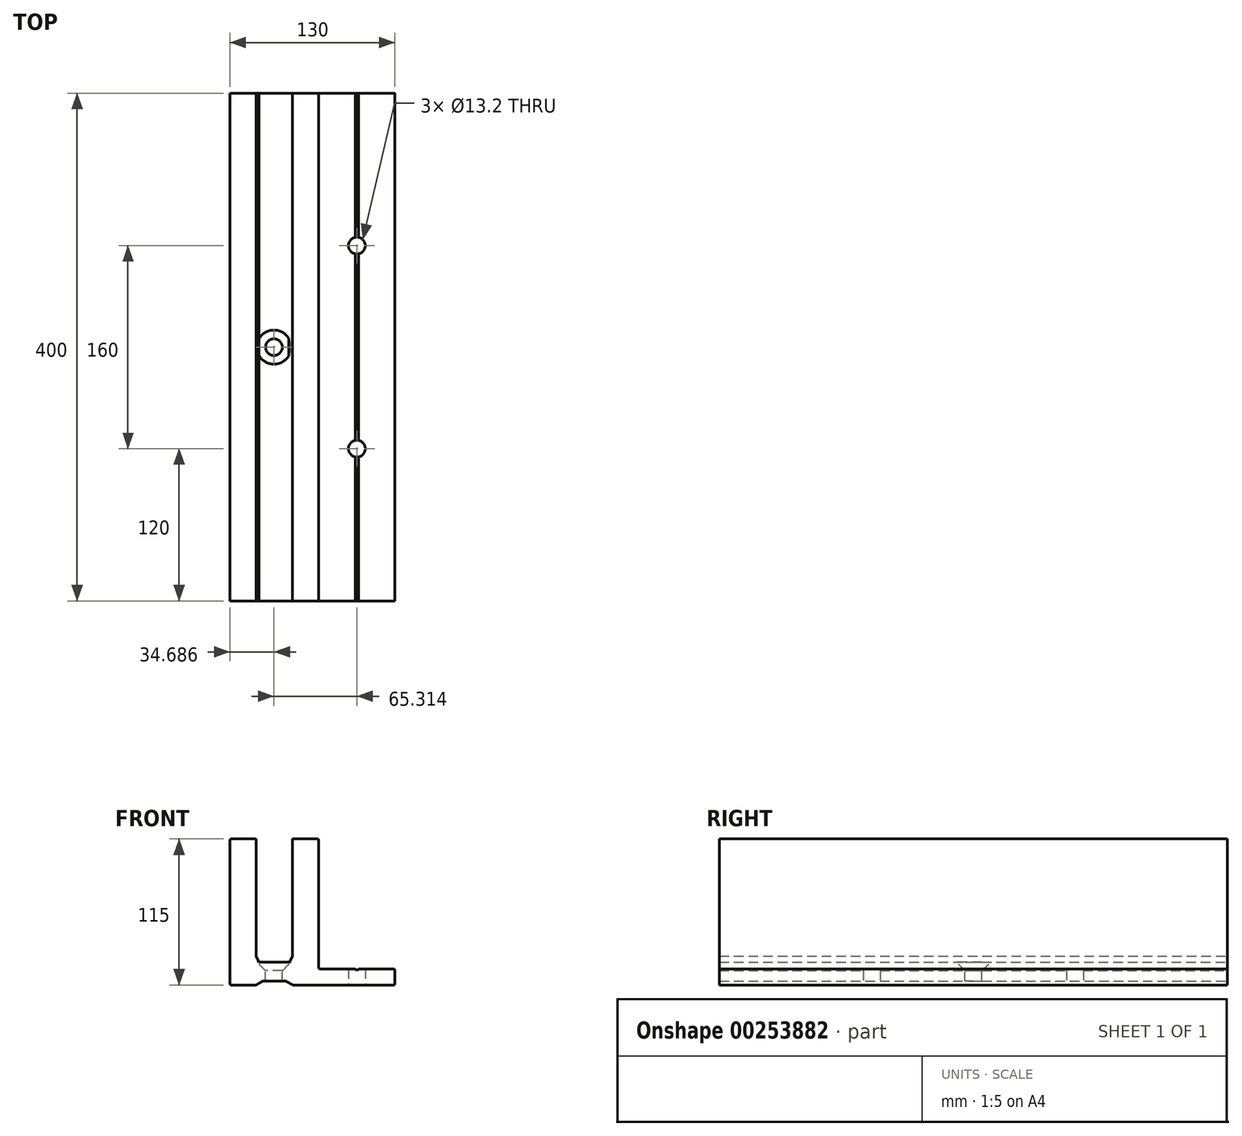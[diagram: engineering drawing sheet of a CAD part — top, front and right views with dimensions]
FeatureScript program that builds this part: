
annotation { "Feature Type Name" : "Feature", "Feature Type Description" : "" }
export const myFeature = defineFeature(function(context is Context, id is Id, definition is map)
    precondition{}
    {
        {
            var Q0;
            Q0=qCreatedBy(makeId("Front.planeOp"),FACE);
            var sketch = newSketch(context, id + "F0", { "sketchPlane" : qUnion([Q0])});
            skLineSegment(sketch, "E0.bottom", {"start": v(1, 0) * mm, "end": v(20.37, 0) * mm});
            skLineSegment(sketch, "E0.top", {"start": v(1, 115) * mm, "end": v(20.65, 115) * mm});
            skLineSegment(sketch, "E0.left", {"start": v(0, 1) * mm, "end": v(0, 114) * mm});
            skLineSegment(sketch, "E0.right", {"start": v(130, 1) * mm, "end": v(130, 11.5) * mm});
            skLineSegment(sketch, "E1", {"start": v(70, 114) * mm, "end": v(70, 13.5) * mm});
            skLineSegment(sketch, "E2.0", {"start": v(20.65, 22.86) * mm, "end": v(20.65, 115) * mm});
            skLineSegment(sketch, "E3.0", {"start": v(49.35, 115) * mm, "end": v(49.35, 23.1) * mm});
            skLineSegment(sketch, "E4.0", {"start": v(23, 18) * mm, "end": v(46.37, 18) * mm});
            skLineSegment(sketch, "E5.trimOffspring", {"start": v(71, 12.5) * mm, "end": v(98.8, 12.5) * mm});
            skLineSegment(sketch, "E6.trimOffspring", {"start": v(49.35, 115) * mm, "end": v(69, 115) * mm});
            skLineSegment(sketch, "E7", {"start": v(35, 3) * mm, "end": v(44.07, 3) * mm});
            skPoint(sketch, "E7.startSnap0", {"position": v(35, 18) * mm});
            skLineSegment(sketch, "E8", {"start": v(35, 3) * mm, "end": v(25.93, 3) * mm});
            skLineSegment(sketch, "E9", {"start": v(25.41, 2.86) * mm, "end": v(20.89, 0.14) * mm});
            skLineSegment(sketch, "E10", {"start": v(44.59, 2.86) * mm, "end": v(49.11, 0.14) * mm});
            skLineSegment(sketch, "E11.trimOffspring", {"start": v(49.63, 0) * mm, "end": v(129, 0) * mm});
            skLineSegment(sketch, "E12", {"start": v(20.65, 22.86) * mm, "end": v(23, 18) * mm});
            skLineSegment(sketch, "E13", {"start": v(49.25, 22.66) * mm, "end": v(47.27, 18.56) * mm});
            skPoint(sketch, "E14.orphan", {"position": v(20.65, 18) * mm});
            skPoint(sketch, "E15.orphan", {"position": v(49.35, 18) * mm});
            skPoint(sketch, "E16.visualSharp", {"position": v(0, 115) * mm});
            skArc(sketch, "E16.filletArc", {"start": v(1, 115) * mm, "mid": v(0.3, 114.7) * mm, "end": v(0, 114) * mm});
            skPoint(sketch, "E17.visualSharp", {"position": v(70, 115) * mm});
            skArc(sketch, "E17.filletArc", {"start": v(70, 114) * mm, "mid": v(69.7, 114.7) * mm, "end": v(69, 115) * mm});
            skPoint(sketch, "E18.visualSharp", {"position": v(0, 0) * mm});
            skArc(sketch, "E18.filletArc", {"start": v(0, 1) * mm, "mid": v(0.3, 0.3) * mm, "end": v(1, 0) * mm});
            skPoint(sketch, "E19.visualSharp", {"position": v(20.65, 0) * mm});
            skArc(sketch, "E19.filletArc", {"start": v(20.37, 0) * mm, "mid": v(20.64, 0.04) * mm, "end": v(20.89, 0.14) * mm});
            skPoint(sketch, "E20.visualSharp", {"position": v(25.65, 3) * mm});
            skArc(sketch, "E20.filletArc", {"start": v(25.93, 3) * mm, "mid": v(25.66, 2.96) * mm, "end": v(25.41, 2.86) * mm});
            skPoint(sketch, "E21.visualSharp", {"position": v(44.35, 3) * mm});
            skArc(sketch, "E21.filletArc", {"start": v(44.59, 2.86) * mm, "mid": v(44.34, 2.96) * mm, "end": v(44.07, 3) * mm});
            skPoint(sketch, "E22.visualSharp", {"position": v(49.35, 0) * mm});
            skArc(sketch, "E22.filletArc", {"start": v(49.11, 0.14) * mm, "mid": v(49.36, 0.04) * mm, "end": v(49.63, 0) * mm});
            skPoint(sketch, "E23.visualSharp", {"position": v(70, 12.5) * mm});
            skArc(sketch, "E23.filletArc", {"start": v(70, 13.5) * mm, "mid": v(70.3, 12.8) * mm, "end": v(71, 12.5) * mm});
            skPoint(sketch, "E24.visualSharp", {"position": v(130, 12.5) * mm});
            skArc(sketch, "E24.filletArc", {"start": v(130, 11.5) * mm, "mid": v(129.7, 12.2) * mm, "end": v(129, 12.5) * mm});
            skPoint(sketch, "E25.visualSharp", {"position": v(130, 0) * mm});
            skArc(sketch, "E25.filletArc", {"start": v(129, 0) * mm, "mid": v(129.7, 0.3) * mm, "end": v(130, 1) * mm});
            skPoint(sketch, "E26.visualSharp", {"position": v(49.35, 22.86) * mm});
            skArc(sketch, "E26.filletArc", {"start": v(49.25, 22.66) * mm, "mid": v(49.32, 22.87) * mm, "end": v(49.35, 23.1) * mm});
            skPoint(sketch, "E27.visualSharp", {"position": v(47, 18) * mm});
            skArc(sketch, "E27.filletArc", {"start": v(46.37, 18) * mm, "mid": v(46.9, 18.15) * mm, "end": v(47.27, 18.56) * mm});
            skLineSegment(sketch, "E28", {"start": v(100, 11.3) * mm, "end": v(101.2, 12.5) * mm});
            skLineSegment(sketch, "E29", {"start": v(100, 11.3) * mm, "end": v(98.8, 12.5) * mm});
            skLineSegment(sketch, "E30.trimOffspring", {"start": v(101.2, 12.5) * mm, "end": v(129, 12.5) * mm});
            skPoint(sketch, "E31.start.orphan", {"position": v(100, 12.5) * mm});
            skSolve(sketch);
        }
        {
            var Q0;
            Q0=makeQuery(id+"F0.imprint","IMPRINT",FACE,{"disambiguationData":[TD([[makeQuery(id+"F0.imprint","IMPRINT",EDGE,{"derivedFrom":sQuery(id+"F0.wireOp",EDGE,"E0.bottom")}),1.0]])]});
            extrude(context, id + "F1", {"entities" : qUnion([Q0]), "depth" : 400 * mm});
        }
        {
            var Q0;
            Q0=makeQuery(id+"F1.opExtrude","SWEPT_FACE",FACE,{"disambiguationData":[OSD([sQuery(id+"F0.wireOp",EDGE,"E4.0")])]});
            var sketch = newSketch(context, id + "F2", { "sketchPlane" : qUnion([Q0])});
            skPoint(sketch, "E32", {"position": v(34.69, -200) * mm});
            skPoint(sketch, "E32.positionSnap0", {"position": v(23, -200) * mm});
            skPoint(sketch, "E32.positionSnap1", {"position": v(34.69, 0) * mm});
            skSolve(sketch);
        }
        {
            var Q0;
            Q0=sQuery(id+"F2.wireOp",VERTEX,"E32");
            var Q1;
            Q1=makeQuery(id+"F1.opExtrude","SWEPT_BODY",BODY,{"disambiguationData":[OSD([sQuery(id+"F0.wireOp",EDGE,"E0.bottom"),sQuery(id+"F0.wireOp",EDGE,"E0.top"),sQuery(id+"F0.wireOp",EDGE,"E0.left"),sQuery(id+"F0.wireOp",EDGE,"E0.right"),sQuery(id+"F0.wireOp",EDGE,"E1"),sQuery(id+"F0.wireOp",EDGE,"E2.0"),sQuery(id+"F0.wireOp",EDGE,"E3.0"),sQuery(id+"F0.wireOp",EDGE,"E4.0"),sQuery(id+"F0.wireOp",EDGE,"E5.trimOffspring"),sQuery(id+"F0.wireOp",EDGE,"E6.trimOffspring"),sQuery(id+"F0.wireOp",EDGE,"E7"),sQuery(id+"F0.wireOp",EDGE,"E8"),sQuery(id+"F0.wireOp",EDGE,"E9"),sQuery(id+"F0.wireOp",EDGE,"E10"),sQuery(id+"F0.wireOp",EDGE,"E11.trimOffspring"),sQuery(id+"F0.wireOp",EDGE,"E12"),sQuery(id+"F0.wireOp",EDGE,"E13"),sQuery(id+"F0.wireOp",EDGE,"E16.filletArc"),sQuery(id+"F0.wireOp",EDGE,"E17.filletArc"),sQuery(id+"F0.wireOp",EDGE,"E18.filletArc"),sQuery(id+"F0.wireOp",EDGE,"E19.filletArc"),sQuery(id+"F0.wireOp",EDGE,"E20.filletArc"),sQuery(id+"F0.wireOp",EDGE,"E21.filletArc"),sQuery(id+"F0.wireOp",EDGE,"E22.filletArc"),sQuery(id+"F0.wireOp",EDGE,"E23.filletArc"),sQuery(id+"F0.wireOp",EDGE,"E24.filletArc"),sQuery(id+"F0.wireOp",EDGE,"E25.filletArc"),sQuery(id+"F0.wireOp",EDGE,"E26.filletArc"),sQuery(id+"F0.wireOp",EDGE,"E27.filletArc"),sQuery(id+"F0.wireOp",EDGE,"E28"),sQuery(id+"F0.wireOp",EDGE,"E29"),sQuery(id+"F0.wireOp",EDGE,"E30.trimOffspring")])]});
            hole(context, id + "F3", {"style" : HoleStyle.C_SINK, "endStyle" : HoleEndStyle.BLIND, "standardTappedOrClearance" : lookupTablePath({ "standard" : "ISO", "fit" : "Normal", "size" : "M12", "type" : "Clearance" }), "standardBlindInLast" : lookupTablePath({ "fit" : "Standard", "standard" : "ISO", "size" : "M12", "type" : "Clearance" }), "holeDiameter" : 13.2 * mm, "cSinkDiameter" : 26.88 * mm, "cSinkAngle" : 90 * degree, "holeDepth" : 20 * mm, "tappedDepth" : 12 * mm, "tapClearance" : 3, "locations" : qUnion([Q0]), "scope" : qUnion([Q1])});
        }
        {
            var Q0;
            Q0=makeQuery(id+"F1.opExtrude","SWEPT_FACE",FACE,{"disambiguationData":[OSD([sQuery(id+"F0.wireOp",EDGE,"E11.trimOffspring")])]});
            var sketch = newSketch(context, id + "F4", { "sketchPlane" : qUnion([Q0])});
            skLineSegment(sketch, "E33", {"start": v(100, 200) * mm, "end": v(100, 280) * mm});
            skPoint(sketch, "E33.startSnap0", {"position": v(49.63, 200) * mm});
            skLineSegment(sketch, "E34", {"start": v(100, 200) * mm, "end": v(100, 120) * mm});
            skSolve(sketch);
        }
        {
            var Q0;
            Q0=sQuery(id+"F4.wireOp",VERTEX,"E34.end");
            var Q1;
            Q1=sQuery(id+"F4.wireOp",VERTEX,"E33.end");
            var Q2;
            Q2=makeQuery(id+"F1.opExtrude","SWEPT_BODY",BODY,{"disambiguationData":[OSD([sQuery(id+"F0.wireOp",EDGE,"E0.bottom"),sQuery(id+"F0.wireOp",EDGE,"E0.top"),sQuery(id+"F0.wireOp",EDGE,"E0.left"),sQuery(id+"F0.wireOp",EDGE,"E0.right"),sQuery(id+"F0.wireOp",EDGE,"E1"),sQuery(id+"F0.wireOp",EDGE,"E2.0"),sQuery(id+"F0.wireOp",EDGE,"E3.0"),sQuery(id+"F0.wireOp",EDGE,"E4.0"),sQuery(id+"F0.wireOp",EDGE,"E5.trimOffspring"),sQuery(id+"F0.wireOp",EDGE,"E6.trimOffspring"),sQuery(id+"F0.wireOp",EDGE,"E7"),sQuery(id+"F0.wireOp",EDGE,"E8"),sQuery(id+"F0.wireOp",EDGE,"E9"),sQuery(id+"F0.wireOp",EDGE,"E10"),sQuery(id+"F0.wireOp",EDGE,"E11.trimOffspring"),sQuery(id+"F0.wireOp",EDGE,"E12"),sQuery(id+"F0.wireOp",EDGE,"E13"),sQuery(id+"F0.wireOp",EDGE,"E16.filletArc"),sQuery(id+"F0.wireOp",EDGE,"E17.filletArc"),sQuery(id+"F0.wireOp",EDGE,"E18.filletArc"),sQuery(id+"F0.wireOp",EDGE,"E19.filletArc"),sQuery(id+"F0.wireOp",EDGE,"E20.filletArc"),sQuery(id+"F0.wireOp",EDGE,"E21.filletArc"),sQuery(id+"F0.wireOp",EDGE,"E22.filletArc"),sQuery(id+"F0.wireOp",EDGE,"E23.filletArc"),sQuery(id+"F0.wireOp",EDGE,"E24.filletArc"),sQuery(id+"F0.wireOp",EDGE,"E25.filletArc"),sQuery(id+"F0.wireOp",EDGE,"E26.filletArc"),sQuery(id+"F0.wireOp",EDGE,"E27.filletArc"),sQuery(id+"F0.wireOp",EDGE,"E28"),sQuery(id+"F0.wireOp",EDGE,"E29"),sQuery(id+"F0.wireOp",EDGE,"E30.trimOffspring")])]});
            hole(context, id + "F5", {"style" : HoleStyle.SIMPLE, "endStyle" : HoleEndStyle.BLIND, "standardTappedOrClearance" : lookupTablePath({ "standard" : "ISO", "fit" : "Normal", "size" : "M12", "type" : "Clearance" }), "standardBlindInLast" : lookupTablePath({ "fit" : "Standard", "standard" : "ISO", "size" : "M12", "type" : "Clearance" }), "holeDiameter" : 13.2 * mm, "holeDepth" : 20 * mm, "tappedDepth" : 12 * mm, "tapClearance" : 3, "locations" : qUnion([Q0, Q1]), "scope" : qUnion([Q2])});
        }
    });
